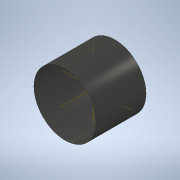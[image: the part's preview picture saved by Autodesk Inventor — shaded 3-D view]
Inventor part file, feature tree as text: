
AUTODESK INVENTOR PART (.ipt)
format: ipt  version: 2020 (Build 240168000, 168)  size: 119,296 bytes
history: native  units: in
note: dims shown in document units (in); Inventor stores cm internally (conversion verified against a paired STEP export)
features: revolve x1, sketch x1
ambient origin geometry x8: Origin, YZ Plane, XZ Plane, XY Plane, X Axis, Y Axis, Z Axis, Center Point
bodies: Solid1 (feature_tree)
feature tree (2):
  revolve  "Revolution1"  [1 undecoded]
  sketch  "Sketch2"  dims[d0=314.9606in d1=16.1417in d2=314.3307in d3=2.3622in d4=1.3386in d5=0.6299in d6=196.8504in d7=0.0in d8=90.0deg d10=136.8213in]
note: 1 required parameter value undecoded (feature->parameter linkage not recoverable at this tier; creation-order binding heuristic only, values carry confidence <= 0.55)
